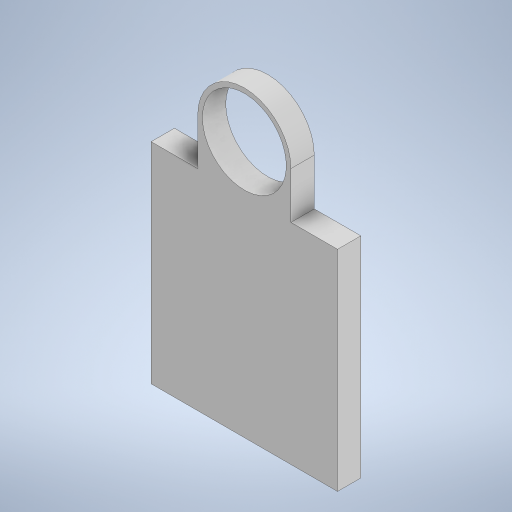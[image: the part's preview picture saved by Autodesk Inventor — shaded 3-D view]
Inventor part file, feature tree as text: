
AUTODESK INVENTOR PART (.ipt)
format: ipt  version: 2024 (Build 280153000, 153)  size: 238,080 bytes
history: native  units: mm
features: sketch x2, other x1, extrude x1, hole x1
ambient origin geometry x8: Origin, YZ Plane, XZ Plane, XY Plane, X Axis, Y Axis, Z Axis, Center Point
bodies: Body1 (feature_tree)
feature tree (5):
  other  "Sólido1"
  extrude  "Extrusión1"  Depth=40.0mm
  hole  "Agujero1"  [1 undecoded]
  sketch  "Boceto1"  dims[d0=36.0mm d1=40.0mm]
  sketch  "Boceto2"  dims[d2=40.0mm d3=10.0mm d4=40.0mm d5=80.0mm d7=10.0mm d8=0.0mm d9=36.0mm d10=36.0mm d11=6.0mm d12=4.0mm d13=2.0mm d14=90.0deg d15=10.0mm d16=20.594885mm]
note: 1 required parameter value undecoded (feature->parameter linkage not recoverable at this tier; creation-order binding heuristic only, values carry confidence <= 0.55)
